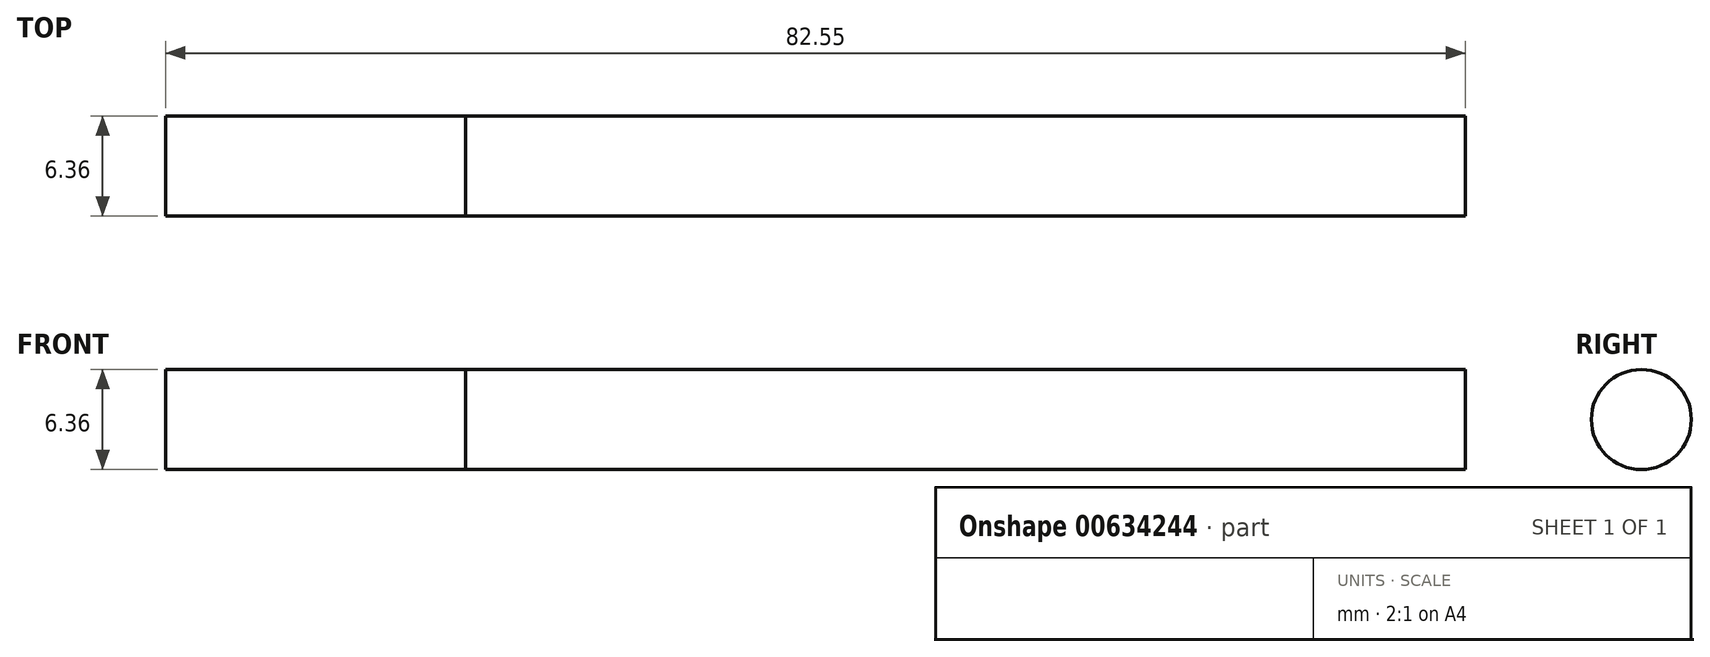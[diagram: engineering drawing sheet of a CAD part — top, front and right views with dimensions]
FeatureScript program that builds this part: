
annotation { "Feature Type Name" : "Feature", "Feature Type Description" : "" }
export const myFeature = defineFeature(function(context is Context, id is Id, definition is map)
    precondition{}
    {
        {
            var Q0;
            Q0=qCreatedBy(makeId("Right.planeOp"),FACE);
            var sketch = newSketch(context, id + "F0", { "sketchPlane" : qUnion([Q0])});
            skCircle(sketch, "E0", {"center": v(0, 0) * mm, "radius": 3.18 * mm});
            skSolve(sketch);
        }
        {
            var Q0;
            Q0 = qSketchRegion(id + "F0", true);
            extrude(context, id + "F1", {"entities" : qUnion([Q0]), "depth" : 82.55 * mm, "offsetDistance" : 25.4 * mm});
        }
        {
            var Q0;
            Q0 = qSketchRegion(id + "F0", true);
            extrude(context, id + "F2", {"entities" : qUnion([Q0]), "depth" : 19.05 * mm, "offsetDistance" : 25.4 * mm});
        }
    });
